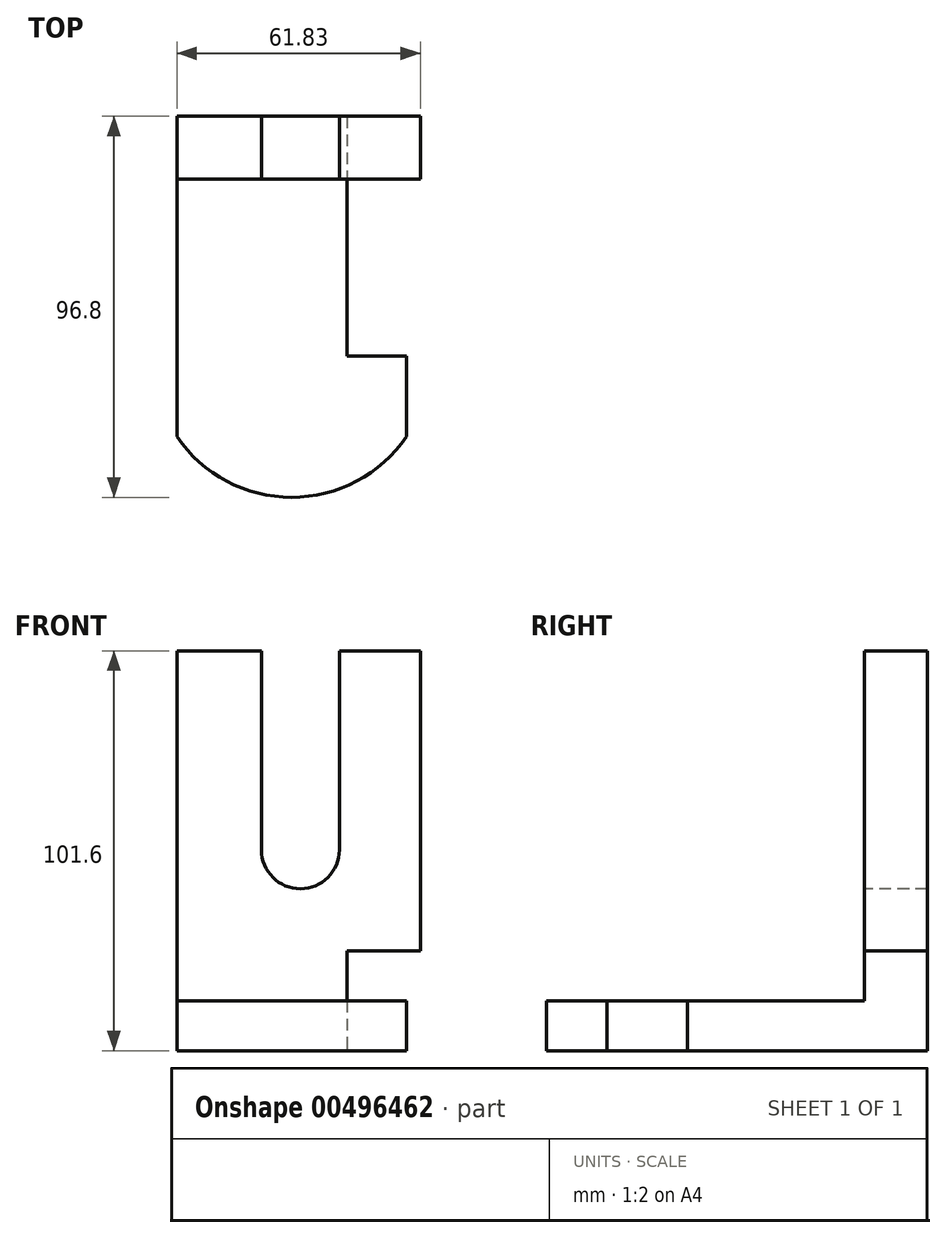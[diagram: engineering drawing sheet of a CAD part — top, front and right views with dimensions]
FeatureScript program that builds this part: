
annotation { "Feature Type Name" : "Feature", "Feature Type Description" : "" }
export const myFeature = defineFeature(function(context is Context, id is Id, definition is map)
    precondition{}
    {
        {
            var Q0;
            Q0=qCreatedBy(makeId("Top.planeOp"),FACE);
            var sketch = newSketch(context, id + "F0", { "sketchPlane" : qUnion([Q0])});
            skLineSegment(sketch, "E0.bottom", {"start": v(-29.59, 41.86) * mm, "end": v(13.58, 41.86) * mm});
            skLineSegment(sketch, "E0.left", {"start": v(-29.59, 41.86) * mm, "end": v(-29.59, -19.04) * mm});
            skLineSegment(sketch, "E0.right", {"start": v(13.58, 41.86) * mm, "end": v(13.58, -19.04) * mm});
            skLineSegment(sketch, "E1.bottom", {"start": v(13.58, -19.04) * mm, "end": v(28.72, -19.04) * mm});
            skLineSegment(sketch, "E1.left", {"start": v(-29.59, -19.04) * mm, "end": v(-29.59, -39.53) * mm});
            skLineSegment(sketch, "E1.right", {"start": v(28.72, -19.04) * mm, "end": v(28.72, -39.53) * mm});
            skArc(sketch, "E2", {"start": v(-29.59, -39.53) * mm, "mid": v(-0.44, -54.94) * mm, "end": v(28.72, -39.53) * mm});
            skSolve(sketch);
        }
        {
            var Q0;
            Q0=makeQuery(id+"F0.imprint","IMPRINT",FACE,{"disambiguationData":[TD([[makeQuery(id+"F0.imprint","IMPRINT",EDGE,{"derivedFrom":sQuery(id+"F0.wireOp",EDGE,"E0.bottom")}),-1.0]])]});
            extrude(context, id + "F1", {"entities" : qUnion([Q0]), "depth" : 12.7 * mm});
        }
        {
            var Q0;
            Q0=makeQuery(id+"F1.opExtrude","CAP_FACE",FACE,{"disambiguationData":[OSD([sQuery(id+"F0.wireOp",EDGE,"E0.bottom"),sQuery(id+"F0.wireOp",EDGE,"E0.left"),sQuery(id+"F0.wireOp",EDGE,"E0.right"),sQuery(id+"F0.wireOp",EDGE,"E1.bottom"),sQuery(id+"F0.wireOp",EDGE,"E1.left"),sQuery(id+"F0.wireOp",EDGE,"E1.right"),sQuery(id+"F0.wireOp",EDGE,"E2")])],"isStart":false});
            var sketch = newSketch(context, id + "F2", { "sketchPlane" : qUnion([Q0])});
            skLineSegment(sketch, "E3.bottom", {"start": v(-29.59, 41.86) * mm, "end": v(13.58, 41.86) * mm});
            skLineSegment(sketch, "E3.top", {"start": v(-29.59, 25.9) * mm, "end": v(13.58, 25.9) * mm});
            skLineSegment(sketch, "E3.left", {"start": v(-29.59, 41.86) * mm, "end": v(-29.59, 25.9) * mm});
            skLineSegment(sketch, "E3.right", {"start": v(13.58, 41.86) * mm, "end": v(13.58, 25.9) * mm});
            skSolve(sketch);
        }
        {
            var Q0;
            Q0 = qSketchRegion(id + "F2", true);
            extrude(context, id + "F3", {"entities" : qUnion([Q0]), "operationType" : NewBodyOperationType.ADD, "depth" : 12.7 * mm});
        }
        {
            var Q0;
            Q0=makeQuery(id+"F3.opExtrude","CAP_FACE",FACE,{"disambiguationData":[OSD([sQuery(id+"F2.wireOp",EDGE,"E3.bottom"),sQuery(id+"F2.wireOp",EDGE,"E3.top"),sQuery(id+"F2.wireOp",EDGE,"E3.left"),sQuery(id+"F2.wireOp",EDGE,"E3.right")])],"isStart":false});
            var sketch = newSketch(context, id + "F4", { "sketchPlane" : qUnion([Q0])});
            skPoint(sketch, "E4.oppositeSnap0", {"position": v(-8, 25.9) * mm});
            skLineSegment(sketch, "E4.bottom", {"start": v(-29.59, 41.86) * mm, "end": v(32.24, 41.86) * mm});
            skLineSegment(sketch, "E4.top", {"start": v(-29.59, 25.9) * mm, "end": v(32.24, 25.9) * mm});
            skLineSegment(sketch, "E4.left", {"start": v(-29.59, 41.86) * mm, "end": v(-29.59, 25.9) * mm});
            skLineSegment(sketch, "E4.right", {"start": v(32.24, 41.86) * mm, "end": v(32.24, 25.9) * mm});
            skSolve(sketch);
        }
        {
            var Q0;
            Q0 = qSketchRegion(id + "F4", true);
            extrude(context, id + "F5", {"entities" : qUnion([Q0]), "operationType" : NewBodyOperationType.ADD, "depth" : 76.2 * mm});
        }
        {
            var Q0;
            Q0=makeQuery(id+"F5.boolean.opBoolean","MERGE",FACE,{"derivedFrom":[makeQuery(id+"F3.opExtrude","SWEPT_FACE",FACE,{"disambiguationData":[OSD([sQuery(id+"F2.wireOp",EDGE,"E3.top")])]}),makeQuery(id+"F5.opExtrude","SWEPT_FACE",FACE,{"disambiguationData":[OSD([sQuery(id+"F4.wireOp",EDGE,"E4.top")])]})]});
            var sketch = newSketch(context, id + "F6", { "sketchPlane" : qUnion([Q0])});
            skLineSegment(sketch, "E5.bottom", {"start": v(-8.11, 101.6) * mm, "end": v(11.7, 101.6) * mm});
            skLineSegment(sketch, "E5.left", {"start": v(-8.11, 101.6) * mm, "end": v(-8.11, 51.02) * mm});
            skLineSegment(sketch, "E5.right", {"start": v(11.7, 101.6) * mm, "end": v(11.7, 51.02) * mm});
            skArc(sketch, "E6", {"start": v(-8.11, 51.02) * mm, "mid": v(1.79, 41.12) * mm, "end": v(11.7, 51.02) * mm});
            skSolve(sketch);
        }
        {
            var Q0;
            Q0 = qSketchRegion(id + "F6", true);
            extrude(context, id + "F7", {"entities" : qUnion([Q0]), "operationType" : NewBodyOperationType.REMOVE, "oppositeDirection" : true, "depth" : 25.4 * mm});
        }
    });
